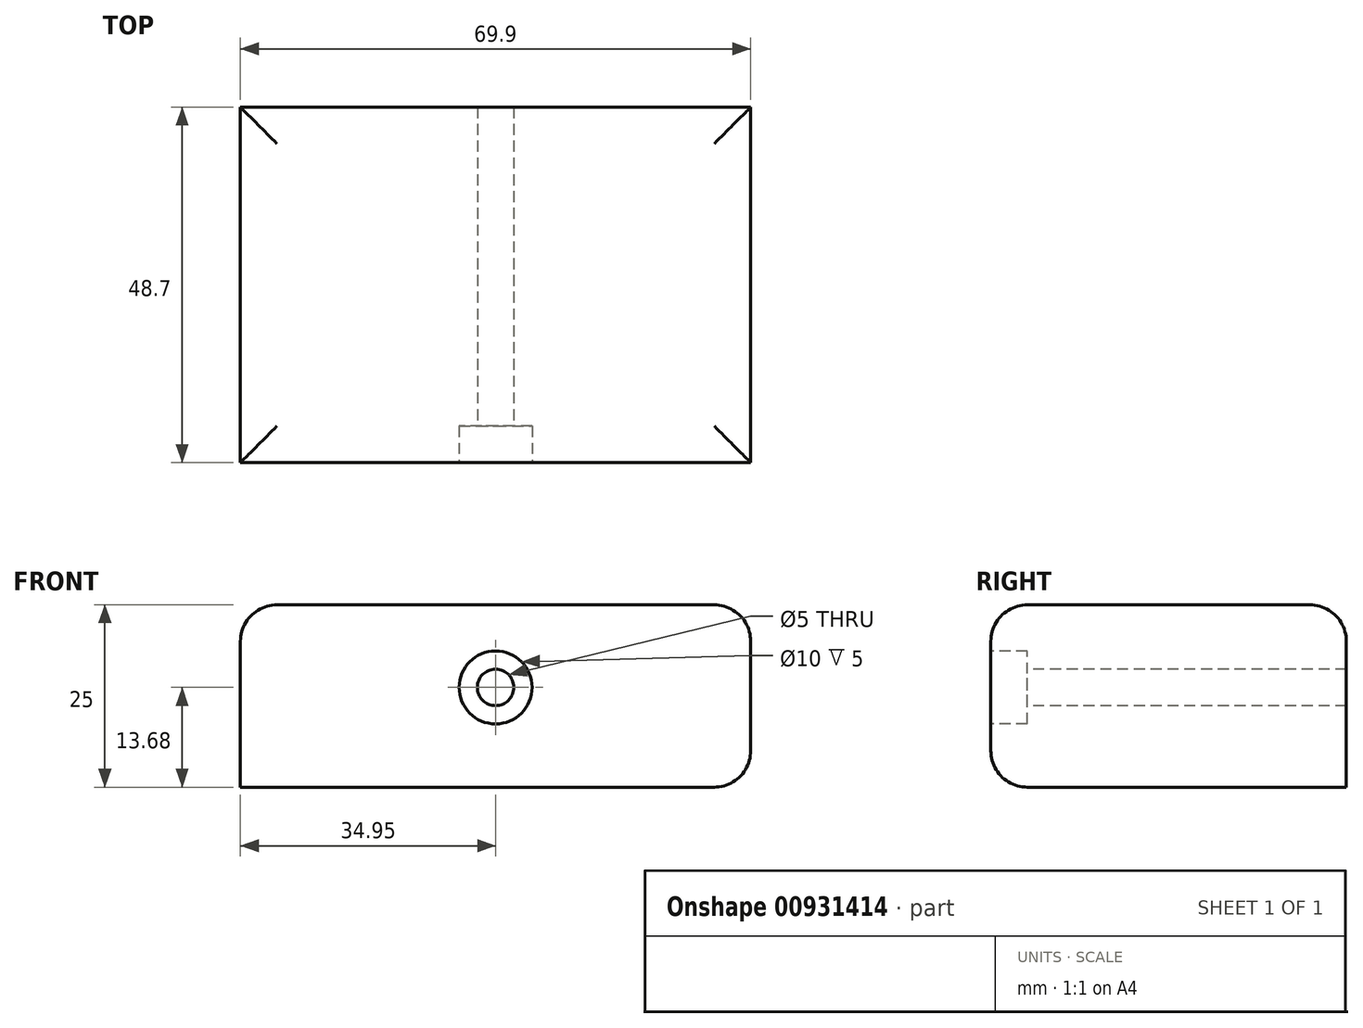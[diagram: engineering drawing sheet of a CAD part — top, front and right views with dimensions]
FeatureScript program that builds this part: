
annotation { "Feature Type Name" : "Feature", "Feature Type Description" : "" }
export const myFeature = defineFeature(function(context is Context, id is Id, definition is map)
    precondition{}
    {
        {
            var Q0;
            Q0=qCreatedBy(makeId("Top.planeOp"),FACE);
            var sketch = newSketch(context, id + "F0", { "sketchPlane" : qUnion([Q0])});
            skLineSegment(sketch, "E0.bottom", {"start": v(-34.95, 24.35) * mm, "end": v(34.95, 24.35) * mm});
            skLineSegment(sketch, "E0.top", {"start": v(-34.95, -24.35) * mm, "end": v(34.95, -24.35) * mm});
            skLineSegment(sketch, "E0.left", {"start": v(-34.95, 24.35) * mm, "end": v(-34.95, -24.35) * mm});
            skLineSegment(sketch, "E0.right", {"start": v(34.95, 24.35) * mm, "end": v(34.95, -24.35) * mm});
            skPoint(sketch, "E0.middle", {"position": v(0, 0) * mm});
            skSolve(sketch);
        }
        {
            var Q0;
            Q0=makeQuery(id+"F0.imprint","IMPRINT",FACE,{"disambiguationData":[TD([[makeQuery(id+"F0.imprint","IMPRINT",EDGE,{"derivedFrom":sQuery(id+"F0.wireOp",EDGE,"E0.bottom")}),-1.0]])]});
            extrude(context, id + "F1", {"entities" : qUnion([Q0]), "depth" : 25 * mm, "offsetDistance" : 25 * mm});
        }
        {
            var Q0;
            Q0=makeQuery(id+"F1.opExtrude","CAP_EDGE",EDGE,{"disambiguationData":[OSD([sQuery(id+"F0.wireOp",EDGE,"E0.bottom")])],"isStart":false});
            var Q1;
            Q1=makeQuery(id+"F1.opExtrude","CAP_EDGE",EDGE,{"disambiguationData":[OSD([sQuery(id+"F0.wireOp",EDGE,"E0.right")])],"isStart":false});
            var Q2;
            Q2=makeQuery(id+"F1.opExtrude","CAP_EDGE",EDGE,{"disambiguationData":[OSD([sQuery(id+"F0.wireOp",EDGE,"E0.top")])],"isStart":false});
            var Q3;
            Q3=makeQuery(id+"F1.opExtrude","CAP_EDGE",EDGE,{"disambiguationData":[OSD([sQuery(id+"F0.wireOp",EDGE,"E0.left")])],"isStart":false});
            var Q4;
            Q4=makeQuery(id+"F1.opExtrude","CAP_EDGE",EDGE,{"disambiguationData":[OSD([sQuery(id+"F0.wireOp",EDGE,"E0.top")])],"isStart":true});
            var Q5;
            Q5=makeQuery(id+"F1.opExtrude","CAP_EDGE",EDGE,{"disambiguationData":[OSD([sQuery(id+"F0.wireOp",EDGE,"E0.right")])],"isStart":true});
            fillet(context, id + "F2", {"entities" : qUnion([Q0, Q1, Q2, Q3, Q4, Q5]), "radius" : 5 * mm, "tangentPropagation" : true, "allowEdgeOverflow" : false});
        }
        {
            var Q0;
            Q0=makeQuery(id+"F1.opExtrude","SWEPT_FACE",FACE,{"disambiguationData":[OSD([sQuery(id+"F0.wireOp",EDGE,"E0.top")])]});
            var sketch = newSketch(context, id + "F3", { "sketchPlane" : qUnion([Q0])});
            skPoint(sketch, "E1", {"position": v(0, 13.68) * mm});
            skSolve(sketch);
        }
        {
            var Q0;
            Q0=sQuery(id+"F3.wireOp",VERTEX,"E1");
            var Q1;
            Q1=makeQuery(id+"F1.opExtrude","SWEPT_BODY",BODY,{"disambiguationData":[OSD([sQuery(id+"F0.wireOp",EDGE,"E0.bottom"),sQuery(id+"F0.wireOp",EDGE,"E0.top"),sQuery(id+"F0.wireOp",EDGE,"E0.left"),sQuery(id+"F0.wireOp",EDGE,"E0.right")])]});
            hole(context, id + "F4", {"style" : HoleStyle.C_BORE, "endStyle" : HoleEndStyle.THROUGH, "holeDiameter" : 5 * mm, "cBoreDiameter" : 10 * mm, "cBoreDepth" : 5 * mm, "majorDiameter" : 5 * mm, "isTappedThrough" : true, "tappedDepth" : 12 * mm, "tapClearance" : 3, "locations" : qUnion([Q0]), "scope" : qUnion([Q1])});
        }
    });
